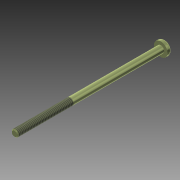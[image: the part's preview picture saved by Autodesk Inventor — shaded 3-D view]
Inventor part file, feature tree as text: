
AUTODESK INVENTOR PART (.ipt)
format: ipt  version: 2018 (Build 220112000, 112)  size: 116,224 bytes
history: native  units: mm
features: imported_body x1, thread x1
ambient origin geometry x8: Origin, YZ Plane, XZ Plane, XY Plane, X Axis, Y Axis, Z Axis, Center Point
bodies: Solid1 (feature_tree)
feature tree (2):
  imported_body  "Base1"
  thread  "Thread1"  [1 undecoded]
note: 1 required parameter value undecoded (feature->parameter linkage not recoverable at this tier; creation-order binding heuristic only, values carry confidence <= 0.55)
